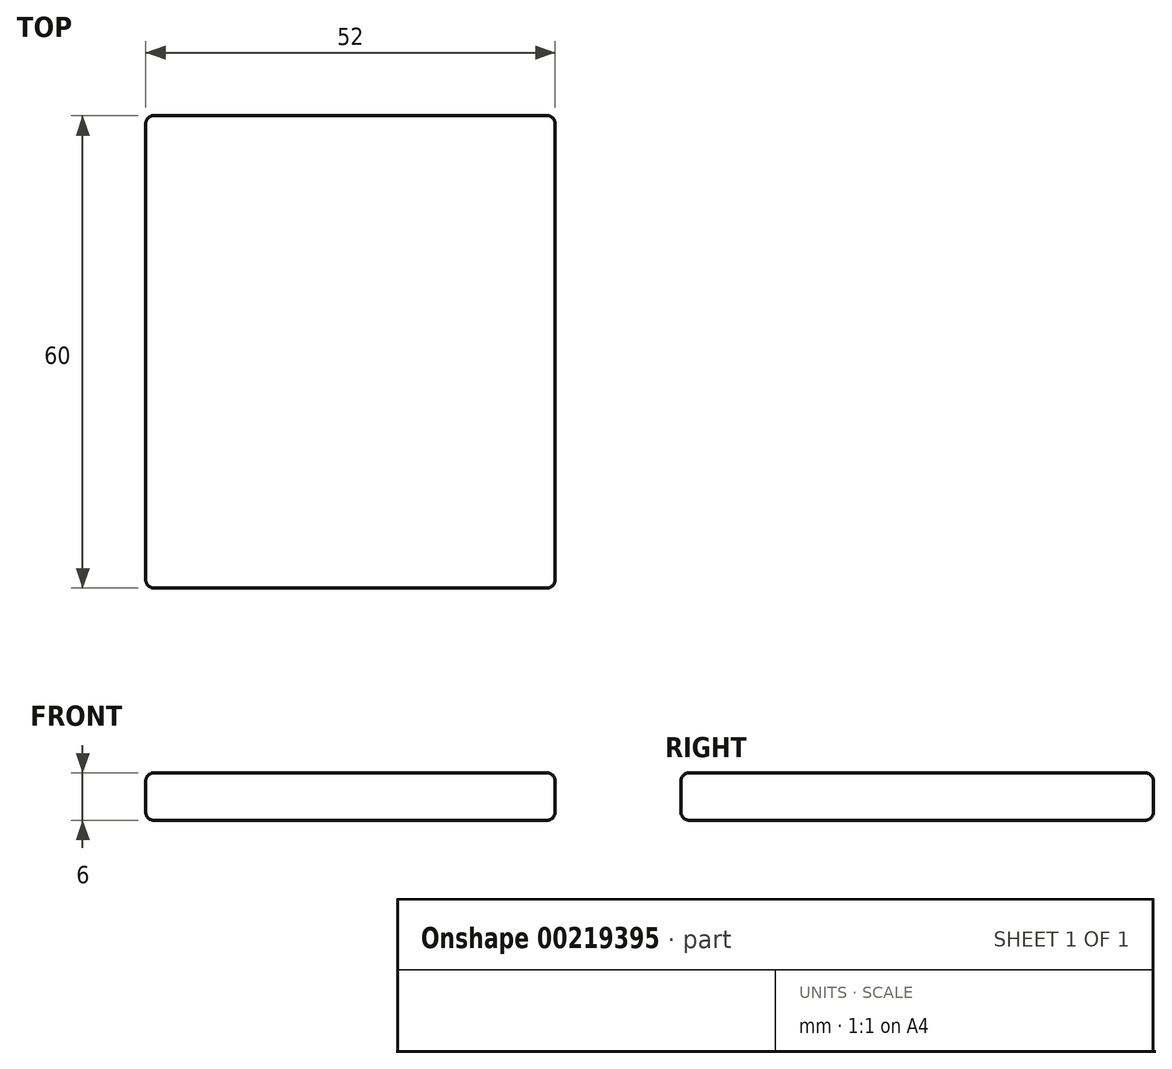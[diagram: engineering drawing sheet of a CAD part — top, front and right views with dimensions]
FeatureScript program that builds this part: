
annotation { "Feature Type Name" : "Feature", "Feature Type Description" : "" }
export const myFeature = defineFeature(function(context is Context, id is Id, definition is map)
    precondition{}
    {
        {
            var Q0;
            Q0=qCreatedBy(makeId("Front.planeOp"),FACE);
            var sketch = newSketch(context, id + "F0", { "sketchPlane" : qUnion([Q0])});
            skLineSegment(sketch, "E0", {"start": v(-26, 0) * mm, "end": v(26, 0) * mm});
            skLineSegment(sketch, "E1.top", {"start": v(-26, 6) * mm, "end": v(26, 6) * mm});
            skLineSegment(sketch, "E1.left", {"start": v(-26, 0) * mm, "end": v(-26, 6) * mm});
            skLineSegment(sketch, "E1.right", {"start": v(26, 0) * mm, "end": v(26, 6) * mm});
            skPoint(sketch, "E2", {"position": v(0, 0) * mm});
            skSolve(sketch);
        }
        {
            var Q0;
            Q0=makeQuery(id+"F0.imprint","IMPRINT",FACE,{"disambiguationData":[TD([[makeQuery(id+"F0.imprint","IMPRINT",EDGE,{"derivedFrom":sQuery(id+"F0.wireOp",EDGE,"E0")}),1.0]])]});
            extrude(context, id + "F1", {"entities" : qUnion([Q0]), "oppositeDirection" : true, "depth" : 60 * mm});
        }
        {
            var Q0;
            Q0=makeQuery(id+"F1.opExtrude","CAP_EDGE",EDGE,{"disambiguationData":[OSD([sQuery(id+"F0.wireOp",EDGE,"E1.top")])],"isStart":false});
            var Q1;
            Q1=makeQuery(id+"F1.opExtrude","SWEPT_FACE",FACE,{"disambiguationData":[OSD([sQuery(id+"F0.wireOp",EDGE,"E1.top")])]});
            var Q2;
            Q2=makeQuery(id+"F1.opExtrude","CAP_EDGE",EDGE,{"disambiguationData":[OSD([sQuery(id+"F0.wireOp",EDGE,"E1.right")])],"isStart":false});
            var Q3;
            Q3=makeQuery(id+"F1.opExtrude","SWEPT_EDGE",EDGE,{"disambiguationData":[OSD([sQuery(id+"F1l0F6nsCicgE8X_1.wireOp",EDGE,"wpPDarrE-2ddr-bAHx-TX1n-N1GLBXqXS2so"),sQuery(id+"FGOJZNfot3GXA15_2.wireOp",EDGE,"IZuoqtNz-5W7o-dHhf-4Erc-ZDTHIUvWr0XE.top"),sQuery(id+"F0.wireOp",EDGE,"E0"),sQuery(id+"F0.wireOp",EDGE,"E1.left")])]});
            var Q4;
            Q4=makeQuery(id+"F1.opExtrude","CAP_EDGE",EDGE,{"disambiguationData":[OSD([sQuery(id+"F0.wireOp",EDGE,"E1.left")])],"isStart":false});
            var Q5;
            Q5=makeQuery(id+"F1.opExtrude","CAP_EDGE",EDGE,{"disambiguationData":[OSD([sQuery(id+"F0.wireOp",EDGE,"E0")])],"isStart":false});
            var Q6;
            Q6=makeQuery(id+"F1.opExtrude","SWEPT_FACE",FACE,{"disambiguationData":[OSD([sQuery(id+"F0.wireOp",EDGE,"E0")])]});
            var Q7;
            Q7=makeQuery(id+"F1.opExtrude","CAP_FACE",FACE,{"disambiguationData":[OSD([sQuery(id+"F0.wireOp",EDGE,"E0"),sQuery(id+"F0.wireOp",EDGE,"E1.top"),sQuery(id+"F0.wireOp",EDGE,"E1.left"),sQuery(id+"F0.wireOp",EDGE,"E1.right")])],"isStart":true});
            fillet(context, id + "F2", {"entities" : qUnion([Q0, Q1, Q2, Q3, Q4, Q5, Q6, Q7]), "radius" : 1 * mm, "tangentPropagation" : true, "allowEdgeOverflow" : false});
        }
    });
